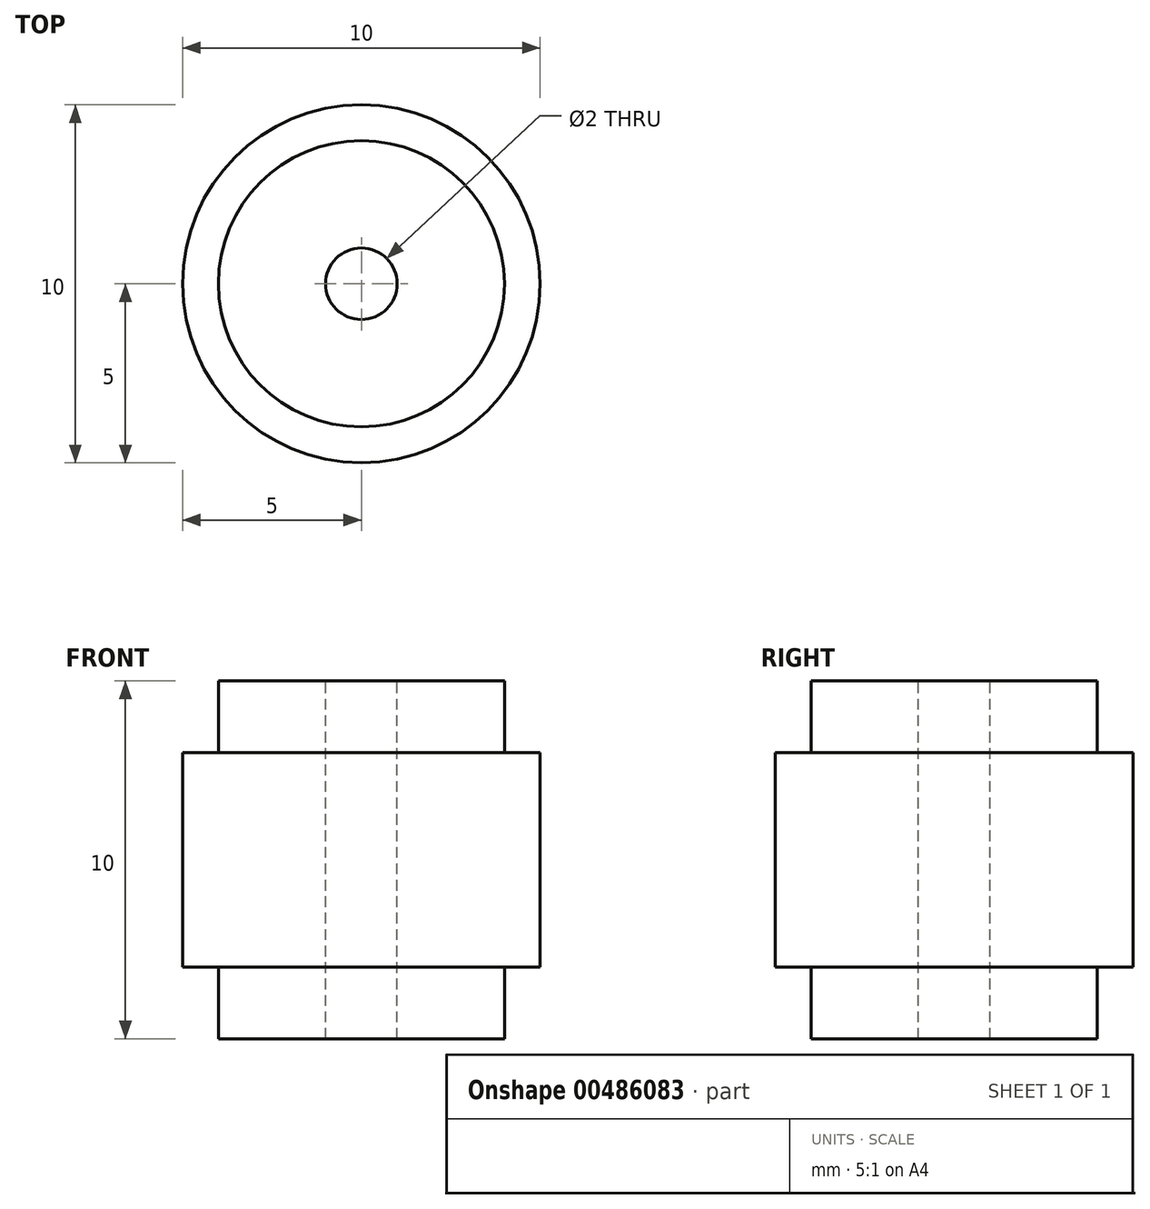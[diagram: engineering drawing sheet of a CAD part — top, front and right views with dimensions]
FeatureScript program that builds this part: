
annotation { "Feature Type Name" : "Feature", "Feature Type Description" : "" }
export const myFeature = defineFeature(function(context is Context, id is Id, definition is map)
    precondition{}
    {
        {
            var Q0;
            Q0=qCreatedBy(makeId("Front.planeOp"),FACE);
            var sketch = newSketch(context, id + "F0", { "sketchPlane" : qUnion([Q0])});
            skLineSegment(sketch, "E0.top", {"start": v(-1, -5) * mm, "end": v(-4, -5) * mm});
            skLineSegment(sketch, "E0.right", {"start": v(-5, 3) * mm, "end": v(-5, -3) * mm});
            skPoint(sketch, "E0.middle", {"position": v(0, 0) * mm});
            skLineSegment(sketch, "E1.right", {"start": v(-1, 5) * mm, "end": v(-1, -5) * mm});
            skLineSegment(sketch, "E2", {"start": v(-5, 3) * mm, "end": v(-4, 3) * mm});
            skLineSegment(sketch, "E3", {"start": v(-4, 3) * mm, "end": v(-4, 5) * mm});
            skLineSegment(sketch, "E4.trimOffspring", {"start": v(-1, 5) * mm, "end": v(-4, 5) * mm});
            skLineSegment(sketch, "E5.bottom", {"start": v(-5, -3) * mm, "end": v(-4, -3) * mm});
            skLineSegment(sketch, "E5.right", {"start": v(-4, -3) * mm, "end": v(-4, -5) * mm});
            skLineSegment(sketch, "E6", {"start": v(0, 0) * mm, "end": v(0, 7.19) * mm, "construction": true});
            skSolve(sketch);
        }
        {
            var Q0;
            Q0 = qConstructionFilter(qBodyType(qCreatedBy(id + "F0" ,EDGE), BodyType.WIRE), ConstructionObject.NO);
            var Q1;
            Q1=sQuery(id+"F0.wireOp",EDGE,"E6");
            revolve(context, id + "F1", {"bodyType" : ToolBodyType.SURFACE, "surfaceEntities" : qUnion([Q0]), "axis" : qUnion([Q1]), "revolveType" : RevolveType.FULL});
        }
    });
